# Revit family: Cooling_Plant-Accessories-Calmac-IceBank-Model-1220C2F
name_source: partatom
category: Mechanical Equipment
revit_build: Autodesk Revit 2014 (Build: 20140709_2115(x64)
units: mm (PartAtom-declared; Revit-internal decimal feet)

## types (1)
- 1220C2F
    Assembly Code = D3030300
    Base Finish = Plastic- Calmac- Black
    Base Height = 125 1/4"
    Body Material = Plastic- Calmac- Off_White
    CTRL Base Radius = 43 1/2"
    CTRL Hydronic Return Description = Hydronic Return
    CTRL Hydronic Supply Description = Hydronic Supply
    CTRL Off = No
    CTRL On = Yes
    Clearance Box Height = 36"
    Description = Off-Peak Cooling System
    Factory Tested Pressure = 1724 kPa
    Floor Loading Weight = 520 lb/sq.ft.
    Heat Exchanger Volume = 205 Gallons
    Inlet Outlet Center Height = 129"
    Is Tank 1 Back Left Connector Visible = No
    Is Tank 1 Back Right Connector Visible = Yes
    Is Tank 1 Front Left Connector Visible = No
    Is Tank 1 Front Right Connector Visible = Yes
    Leg 1 = 46"
    Leg 4 = 45"
    Lid Diameter = 89"
    Lid Type = Cooling_Plant_Accessories-Calmac-IceBank-Lid_C : Lid-C
    Manufacturer = CALMAC Manufacturing Corp.
    Maximum Operating Pressure = 620 kPa
    Maximum Operating Temperature = 77 °F
    Model = 1220C2F
    Operating Weight = 22500.00 lb
    Pipe Material = Plastic- Calmac- Black
    Product Page URL = http://www.calmac.com
    Shipping Weight = 2600.00 lb
    Surface Finish = Plastic- Calmac- Black
    Tank Net Usable Capacity = 98 Ton-Hrs
    URL = http://www.calmac.com
    Warning = Ice tanks are a component in an ice storage system including chillers, pumps, and controls. Contact CALMAC for IceBank® selection support to make sure all system components will work together properly.
    Water_Ice Tank Volume = 2,185 Gallons

## geometry (parser evidence)
native form markers: Blend x12, Sweep x10
no freeform markers — native parametric forms only
